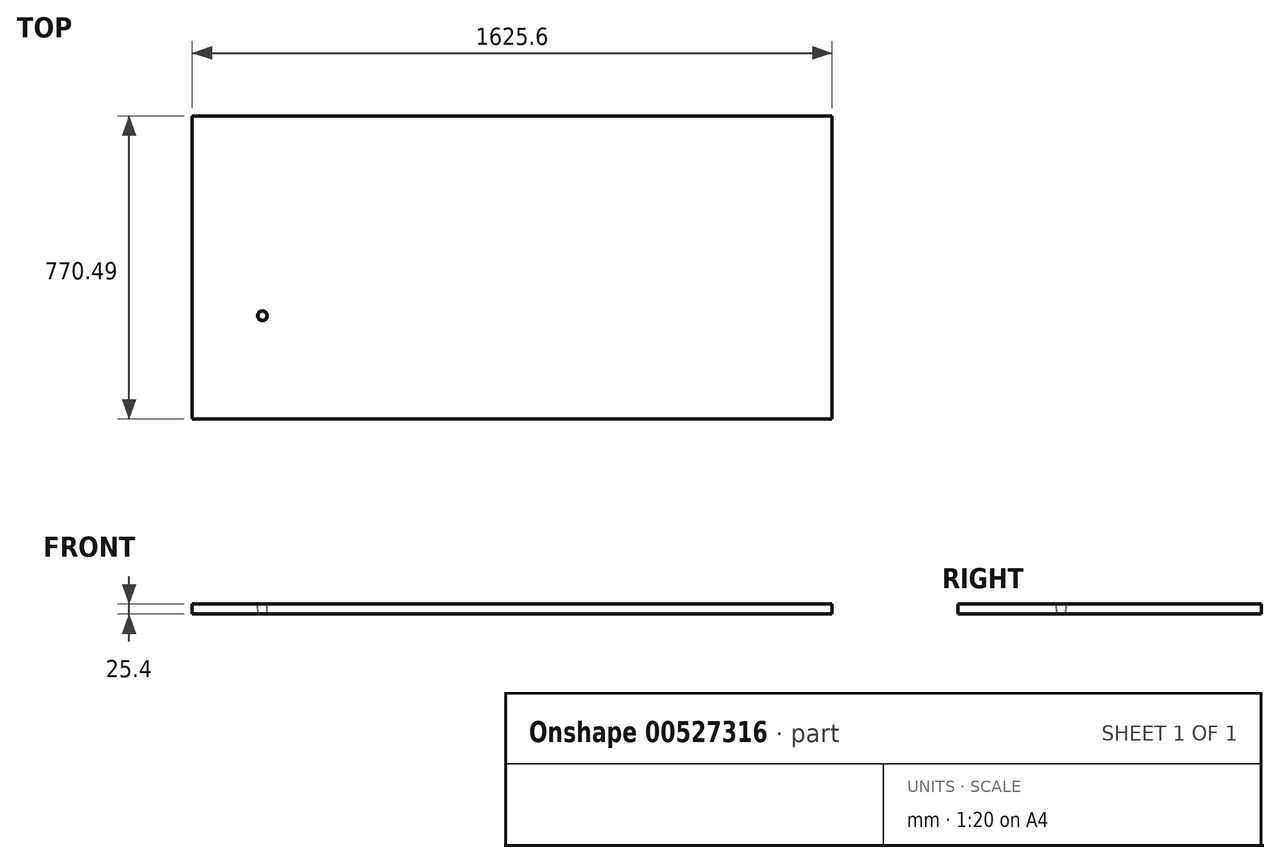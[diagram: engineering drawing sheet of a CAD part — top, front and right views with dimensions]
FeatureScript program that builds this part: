
annotation { "Feature Type Name" : "Feature", "Feature Type Description" : "" }
export const myFeature = defineFeature(function(context is Context, id is Id, definition is map)
    precondition{}
    {
        {
            var Q0;
            Q0=qCreatedBy(makeId("Top.planeOp"),FACE);
            var sketch = newSketch(context, id + "F0", { "sketchPlane" : qUnion([Q0])});
            skSolve(sketch);
        }
        {
            var Q0;
            Q0=qCreatedBy(makeId("Top.planeOp"),FACE);
            var sketch = newSketch(context, id + "F1", { "sketchPlane" : qUnion([Q0])});
            skLineSegment(sketch, "E0.bottom", {"start": v(589.54, 352.52) * mm, "end": v(-1036.06, 352.52) * mm});
            skLineSegment(sketch, "E0.top", {"start": v(589.54, -417.97) * mm, "end": v(-1036.06, -417.97) * mm});
            skLineSegment(sketch, "E0.left", {"start": v(589.54, 352.52) * mm, "end": v(589.54, -417.97) * mm});
            skLineSegment(sketch, "E0.right", {"start": v(-1036.06, 352.52) * mm, "end": v(-1036.06, -417.97) * mm});
            skSolve(sketch);
        }
        {
            var Q0;
            Q0 = qSketchRegion(id + "F1", true);
            extrude(context, id + "F2", {"entities" : qUnion([Q0]), "oppositeDirection" : true, "depth" : 25.4 * mm, "offsetDistance" : 25.4 * mm});
        }
        {
            var Q0;
            Q0=makeQuery(id+"F2.opExtrude","CAP_FACE",FACE,{"disambiguationData":[OSD([sQuery(id+"F1.wireOp",EDGE,"E0.bottom"),sQuery(id+"F1.wireOp",EDGE,"E0.top"),sQuery(id+"F1.wireOp",EDGE,"E0.left"),sQuery(id+"F1.wireOp",EDGE,"E0.right")])],"isStart":true});
            var sketch = newSketch(context, id + "F3", { "sketchPlane" : qUnion([Q0])});
            skFitSpline(sketch, "E1", {"points": [v(-843.97, 190.5) * mm, v(-798.62, 203.93) * mm, v(-777.4, 191.26) * mm, v(-774.35, 159.08) * mm, v(-787.02, 133.26) * mm, v(-800.43, 100.43) * mm, v(-792.5, 66.76) * mm, v(-780.05, 33.13) * mm, v(-763.5, 13.5) * mm, v(-722.91, -20.12) * mm, v(-686.03, -30.15) * mm, v(-657.28, -56.97) * mm, v(-637.96, -57.43) * mm, v(-654.13, -92.05) * mm, v(-645.48, -139.75) * mm, v(-628.27, -168.77) * mm, v(-601.45, -185.74) * mm, v(-597.8, -203.97) * mm, v(-597.88, -235.44) * mm, v(-595.68, -268.82) * mm, v(-591.24, -308.74) * mm, v(-581.25, -340.88) * mm, v(-554.42, -365.33) * mm, v(-514.94, -366.56) * mm, v(-532.34, -342.29) * mm, v(-529.92, -291.85) * mm, v(-519.9, -284.83) * mm, v(-501.93, -255.52) * mm, v(-489.47, -231.73) * mm, v(-485.64, -218.58) * mm, v(-459.83, -207.94) * mm, v(-449.78, -162.87) * mm, v(-435.05, -124.17) * mm, v(-462.3, -100.78) * mm, v(-500.07, -85.77) * mm, v(-519.57, -54.76) * mm, v(-537.8, -48.78) * mm, v(-564.13, -30.62) * mm, v(-593.57, -23.07) * mm, v(-625.28, -28.25) * mm, v(-629.73, -38.37) * mm, v(-651.04, -36.8) * mm, v(-647.73, -12.47) * mm, v(-663.88, -8.87) * mm, v(-660.59, 13.16) * mm, v(-682.62, 24.58) * mm, v(-693.13, 6.1) * mm, v(-705.36, 22.15) * mm, v(-690.91, 45.61) * mm, v(-655.45, 53.94) * mm, v(-645.54, 31.99) * mm, v(-625.22, 33.61) * mm, v(-624.24, 62.27) * mm, v(-603.5, 80.77) * mm, v(-591.64, 92.12) * mm], "startDerivative": vector(2069.76, 1033.65) * mm, "endDerivative": vector(777.33, 1434.89) * mm});
            skFitSpline(sketch, "E2", {"points": [v(-843.97, 190.5) * mm, v(-886.06, 178.23) * mm, v(-924.9, 166.24) * mm, v(-923.33, 180.82) * mm, v(-866.98, 198.55) * mm, v(-866.34, 222.63) * mm], "startDerivative": vector(-176.14, -36.62) * mm, "endDerivative": vector(149.87, 207.15) * mm});
            skFitSpline(sketch, "E3", {"points": [v(-866.34, 222.63) * mm, v(-849.38, 238.08) * mm, v(-798.7, 256.75) * mm, v(-725.1, 258.35) * mm, v(-677.1, 264.22) * mm, v(-621.09, 286.62) * mm, v(-551.74, 296.22) * mm, v(-492, 306.35) * mm, v(-446.13, 309.02) * mm, v(-377.32, 309.55) * mm, v(-309.05, 305.29) * mm, v(-298.91, 293.02) * mm, v(-319.18, 285.02) * mm, v(-337.32, 256.21) * mm, v(-365.05, 239.68) * mm, v(-407.2, 227.94) * mm, v(-428, 205) * mm, v(-458.93, 211.94) * mm, v(-459.47, 245.55) * mm, v(-453.6, 267.95) * mm, v(-476, 271.68) * mm, v(-493.6, 275.42) * mm, v(-505.34, 266.88) * mm, v(-485.6, 252.48) * mm, v(-475.47, 232.74) * mm, v(-492.54, 222.63) * mm, v(-500, 208.74) * mm, v(-496.8, 187.4) * mm, v(-486.67, 173.54) * mm, v(-487.74, 140.47) * mm, v(-514.94, 142.6) * mm, v(-520.8, 133) * mm, v(-544.28, 125) * mm, v(-558.68, 126.6) * mm, v(-565.61, 113.8) * mm, v(-581.08, 110.06) * mm, v(-591.64, 92.12) * mm], "startDerivative": vector(808.27, 621.15) * mm, "endDerivative": vector(-359.8, -927.87) * mm});
            skCircle(sketch, "E4", {"center": v(-798.62, 203.93) * mm, "radius": 12.5 * mm});
            skCircle(sketch, "E5.1.0", {"center": v(222.7, -793.59) * mm, "radius": 12.5 * mm});
            skCircle(sketch, "E5.2.0", {"center": v(575.92, 589.66) * mm, "radius": 12.5 * mm});
            skPoint(sketch, "E5.center", {"position": v(0, 0) * mm});
            skSolve(sketch);
        }
        {
            var Q0;
            Q0=makeQuery(id+"F3.imprint","IMPRINT",FACE,{"disambiguationData":[TD([[makeQuery(id+"F3.imprint","IMPRINT",EDGE,{"derivedFrom":sQuery(id+"F3.wireOp",EDGE,"E1")}),-1.0]])]});
            var sketch = newSketch(context, id + "F4", { "sketchPlane" : qUnion([Q0])});
            skCircle(sketch, "E6", {"center": v(-857.58, -155.35) * mm, "radius": 12.5 * mm});
            skSolve(sketch);
        }
        {
            var Q0;
            Q0 = qSketchRegion(id + "F4", true);
            extrude(context, id + "F5", {"entities" : qUnion([Q0]), "operationType" : NewBodyOperationType.REMOVE, "oppositeDirection" : true, "depth" : 25.4 * mm, "offsetDistance" : 25.4 * mm, "hasDraft" : true, "draftAngle" : 2 * degree, "draftPullDirection" : true});
        }
    });
